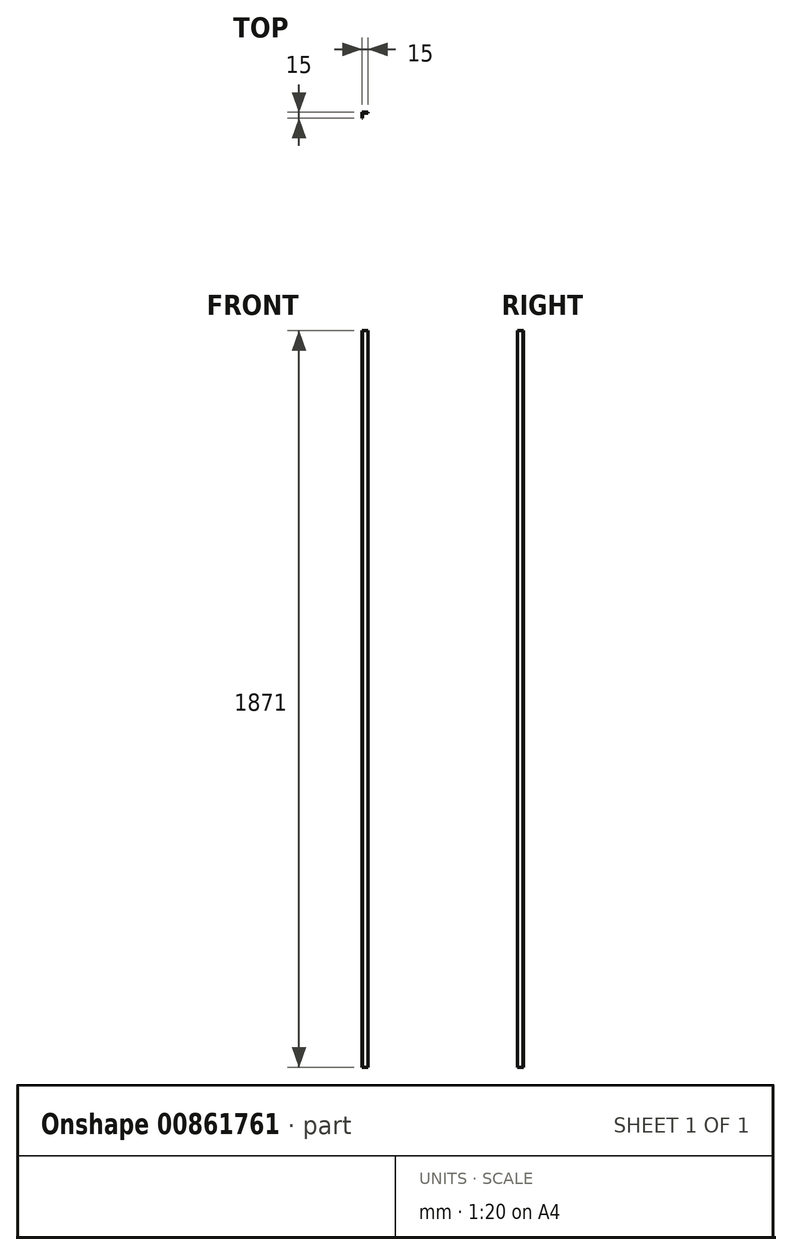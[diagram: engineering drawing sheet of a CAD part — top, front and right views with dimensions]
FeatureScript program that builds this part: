
annotation { "Feature Type Name" : "Feature", "Feature Type Description" : "" }
export const myFeature = defineFeature(function(context is Context, id is Id, definition is map)
    precondition{}
    {
        {
            var Q0;
            Q0=qCreatedBy(makeId("Front.planeOp"),FACE);
            var sketch = newSketch(context, id + "F0", { "sketchPlane" : qUnion([Q0])});
            skLineSegment(sketch, "E0", {"start": v(-21.04, 13.9) * mm, "end": v(-21.04, -1.1) * mm});
            skLineSegment(sketch, "E1", {"start": v(-21.04, -1.1) * mm, "end": v(-6.04, -1.1) * mm});
            skLineSegment(sketch, "E2", {"start": v(-6.04, -1.1) * mm, "end": v(-6.04, 0.5) * mm});
            skLineSegment(sketch, "E3", {"start": v(-6.04, 0.5) * mm, "end": v(-19.44, 0.5) * mm});
            skLineSegment(sketch, "E4", {"start": v(-19.44, 0.5) * mm, "end": v(-19.44, 13.87) * mm});
            skLineSegment(sketch, "E5", {"start": v(-19.44, 13.87) * mm, "end": v(-21.04, 13.9) * mm});
            skSolve(sketch);
        }
        {
            var Q0;
            Q0=makeQuery(id+"F0.imprint","IMPRINT",FACE,{"disambiguationData":[TD([[makeQuery(id+"F0.imprint","IMPRINT",EDGE,{"derivedFrom":sQuery(id+"F0.wireOp",EDGE,"E0")}),1.0]])]});
            extrude(context, id + "F1", {"entities" : qUnion([Q0]), "endBound" : BoundingType.SYMMETRIC, "oppositeDirection" : true, "depth" : 1871 * mm, "offsetDistance" : 25 * mm});
        }
        {
            var Q0;
            Q0=makeQuery(id+"F1.opExtrude","SWEPT_BODY",BODY,{"disambiguationData":[OSD([sQuery(id+"F0.wireOp",EDGE,"E0"),sQuery(id+"F0.wireOp",EDGE,"E1"),sQuery(id+"F0.wireOp",EDGE,"E2"),sQuery(id+"F0.wireOp",EDGE,"E3"),sQuery(id+"F0.wireOp",EDGE,"E4"),sQuery(id+"F0.wireOp",EDGE,"E5")])]});
            var Q1;
            Q1=makeQuery(id+"F1.opExtrude","CAP_EDGE",EDGE,{"disambiguationData":[OSD([sQuery(id+"F0.wireOp",EDGE,"E1")])],"isStart":true});
            transform(context, id + "F2", {"entities" : qUnion([Q0]), "transformType" : TransformType.ROTATION, "transformAxis" : qUnion([Q1]), "angle" : 90 * degree, "makeCopy" : false});
        }
    });
